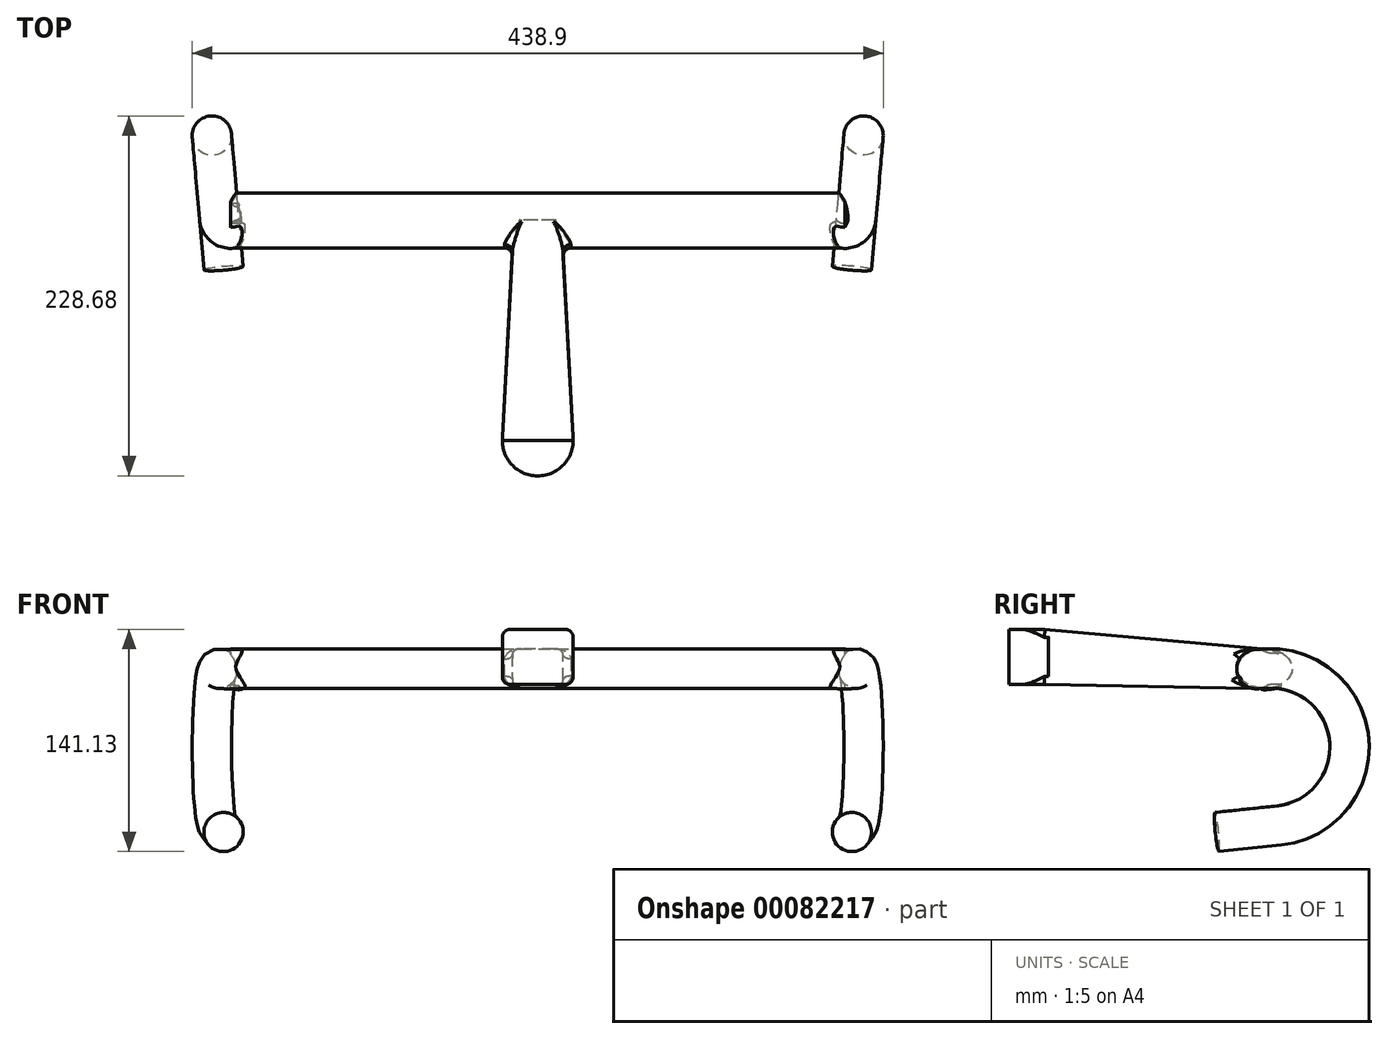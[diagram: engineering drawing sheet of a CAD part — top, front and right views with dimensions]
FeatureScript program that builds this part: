
annotation { "Feature Type Name" : "Feature", "Feature Type Description" : "" }
export const myFeature = defineFeature(function(context is Context, id is Id, definition is map)
    precondition{}
    {
        {
            var Q0;
            Q0=qCreatedBy(makeId("Right.planeOp"),FACE);
            var sketch = newSketch(context, id + "F0", { "sketchPlane" : qUnion([Q0])});
            skLineSegment(sketch, "E0", {"start": v(0, 0) * mm, "end": v(139.8, -7.33) * mm});
            skArc(sketch, "E1", {"start": v(137.2, -107.26) * mm, "mid": v(187.17, -58.57) * mm, "end": v(139.8, -7.33) * mm});
            skLineSegment(sketch, "E2", {"start": v(189.74, -9.94) * mm, "end": v(184.33, -113.2) * mm, "construction": true});
            skLineSegment(sketch, "E3", {"start": v(139.8, -7.33) * mm, "end": v(134.57, -107.19) * mm, "construction": true});
            skLineSegment(sketch, "E4", {"start": v(97.2, -107.26) * mm, "end": v(137.2, -107.26) * mm});
            skSolve(sketch);
        }
        {
            var Q0;
            Q0=qCreatedBy(makeId("Right.planeOp"),FACE);
            cPlane(context, id + "F1", {"entities" : qUnion([Q0]), "cplaneType" : CPlaneType.OFFSET, "offset" : 190 * mm, "width" : 150 * mm, "height" : 150 * mm});
        }
        {
            var Q0;
            Q0=qCreatedBy(makeId("Right.planeOp"),FACE);
            cPlane(context, id + "F2", {"entities" : qUnion([Q0]), "cplaneType" : CPlaneType.OFFSET, "offset" : 190 * mm, "oppositeDirection" : true, "width" : 150 * mm, "height" : 150 * mm});
        }
        {
            var Q0;
            Q0=qCreatedBy(id+"F1.planeOp",FACE);
            var sketch = newSketch(context, id + "F3", { "sketchPlane" : qUnion([Q0])});
            skLineSegment(sketch, "E5", {"start": v(0, 0) * mm, "end": v(139.8, -7.33) * mm});
            skArc(sketch, "E6", {"start": v(137.2, -107.26) * mm, "mid": v(187.17, -58.57) * mm, "end": v(139.8, -7.33) * mm});
            skLineSegment(sketch, "E7", {"start": v(189.74, -9.94) * mm, "end": v(184.33, -113.2) * mm, "construction": true});
            skLineSegment(sketch, "E8", {"start": v(139.8, -7.33) * mm, "end": v(134.57, -107.19) * mm, "construction": true});
            skLineSegment(sketch, "E9", {"start": v(97.2, -107.26) * mm, "end": v(137.2, -107.26) * mm});
            skLineSegment(sketch, "E10", {"start": v(0, 0) * mm, "end": v(0, 35) * mm, "construction": true});
            skSolve(sketch);
        }
        {
            var Q0;
            Q0=qCreatedBy(id+"F2.planeOp",FACE);
            var sketch = newSketch(context, id + "F4", { "sketchPlane" : qUnion([Q0])});
            skLineSegment(sketch, "E11", {"start": v(0, 0) * mm, "end": v(139.8, -7.33) * mm});
            skArc(sketch, "E12", {"start": v(137.2, -107.26) * mm, "mid": v(187.17, -58.57) * mm, "end": v(139.8, -7.33) * mm});
            skLineSegment(sketch, "E13", {"start": v(189.74, -9.94) * mm, "end": v(184.33, -113.2) * mm, "construction": true});
            skLineSegment(sketch, "E14", {"start": v(139.8, -7.33) * mm, "end": v(134.57, -107.19) * mm, "construction": true});
            skLineSegment(sketch, "E15", {"start": v(97.2, -107.26) * mm, "end": v(137.2, -107.26) * mm});
            skLineSegment(sketch, "E16", {"start": v(0, 0) * mm, "end": v(0, 35) * mm, "construction": true});
            skSolve(sketch);
        }
        {
            var Q0;
            Q0=qCreatedBy(id+"F2.planeOp",FACE);
            var Q1;
            Q1=sQuery(id+"F4.wireOp",EDGE,"E16");
            cPlane(context, id + "F5", {"entities" : qUnion([Q0, Q1]), "cplaneType" : CPlaneType.LINE_ANGLE, "offset" : 150 * mm, "angle" : 345 * degree, "width" : 150 * mm, "height" : 150 * mm});
        }
        {
            var Q0;
            Q0=qCreatedBy(id+"F1.planeOp",FACE);
            var Q1;
            Q1=sQuery(id+"F3.wireOp",EDGE,"E10");
            cPlane(context, id + "F6", {"entities" : qUnion([Q0, Q1]), "cplaneType" : CPlaneType.LINE_ANGLE, "offset" : 150 * mm, "angle" : 355 * degree, "width" : 150 * mm, "height" : 150 * mm});
        }
        {
            var Q0;
            Q0=qCreatedBy(makeId("Front.planeOp"),FACE);
            var sketch = newSketch(context, id + "F7", { "sketchPlane" : qUnion([Q0])});
            skLineSegment(sketch, "E17.bottom", {"start": v(22.5, -17.5) * mm, "end": v(-22.5, -17.5) * mm});
            skLineSegment(sketch, "E17.top", {"start": v(22.5, 17.5) * mm, "end": v(-22.5, 17.5) * mm});
            skLineSegment(sketch, "E17.left", {"start": v(22.5, -17.5) * mm, "end": v(22.5, 17.5) * mm});
            skLineSegment(sketch, "E17.right", {"start": v(-22.5, -17.5) * mm, "end": v(-22.5, 17.5) * mm});
            skPoint(sketch, "E17.middle", {"position": v(0, 0) * mm});
            skSolve(sketch);
        }
        {
            var Q0;
            Q0=qCreatedBy(makeId("Front.planeOp"),FACE);
            cPlane(context, id + "F8", {"entities" : qUnion([Q0]), "cplaneType" : CPlaneType.OFFSET, "offset" : 140 * mm, "oppositeDirection" : true, "width" : 150 * mm, "height" : 150 * mm});
        }
        {
            var Q0;
            Q0=qCreatedBy(id+"F8.planeOp",FACE);
            var sketch = newSketch(context, id + "F9", { "sketchPlane" : qUnion([Q0])});
            skLineSegment(sketch, "E18.bottom", {"start": v(15, -19.98) * mm, "end": v(-15, -19.98) * mm});
            skLineSegment(sketch, "E18.top", {"start": v(15, 5.02) * mm, "end": v(-15, 5.02) * mm});
            skLineSegment(sketch, "E18.left", {"start": v(15, -19.98) * mm, "end": v(15, 5.02) * mm});
            skLineSegment(sketch, "E18.right", {"start": v(-15, -19.98) * mm, "end": v(-15, 5.02) * mm});
            skPoint(sketch, "E18.middle", {"position": v(0, -7.48) * mm});
            skSolve(sketch);
        }
        {
            var Q0;
            Q0=makeQuery(id+"F7.imprint","IMPRINT",FACE,{"disambiguationData":[TD([[makeQuery(id+"F7.imprint","IMPRINT",EDGE,{"derivedFrom":sQuery(id+"F7.wireOp",EDGE,"E17.bottom")}),-1.0]])]});
            var Q1;
            Q1=makeQuery(id+"F9.imprint","IMPRINT",FACE,{"disambiguationData":[TD([[makeQuery(id+"F9.imprint","IMPRINT",EDGE,{"derivedFrom":sQuery(id+"F9.wireOp",EDGE,"E18.bottom")}),-1.0]])]});
            loft(context, id + "F10", {"sheetProfilesArray" : [{ "sheetProfileEntities" : qUnion([Q0]) }, { "sheetProfileEntities" : qUnion([Q1]) }]});
        }
        {
            var Q0;
            Q0=makeQuery(id+"F10.opLoft","SWEPT_EDGE",EDGE,{"disambiguationData":[OSD([sQuery(id+"F7.wireOp",EDGE,"E17.top"),sQuery(id+"F7.wireOp",EDGE,"E17.right"),sQuery(id+"F9.wireOp",EDGE,"E18.top"),sQuery(id+"F9.wireOp",EDGE,"E18.right")])]});
            var Q1;
            Q1=makeQuery(id+"F10.opLoft","SWEPT_EDGE",EDGE,{"disambiguationData":[OSD([sQuery(id+"F7.wireOp",EDGE,"E17.top"),sQuery(id+"F7.wireOp",EDGE,"E17.left"),sQuery(id+"F9.wireOp",EDGE,"E18.top"),sQuery(id+"F9.wireOp",EDGE,"E18.left")])]});
            var Q2;
            Q2=makeQuery(id+"F10.opLoft","SWEPT_EDGE",EDGE,{"disambiguationData":[OSD([sQuery(id+"F7.wireOp",EDGE,"E17.bottom"),sQuery(id+"F7.wireOp",EDGE,"E17.left"),sQuery(id+"F9.wireOp",EDGE,"E18.bottom"),sQuery(id+"F9.wireOp",EDGE,"E18.left")])]});
            var Q3;
            Q3=makeQuery(id+"F10.opLoft","SWEPT_EDGE",EDGE,{"disambiguationData":[OSD([sQuery(id+"F7.wireOp",EDGE,"E17.bottom"),sQuery(id+"F7.wireOp",EDGE,"E17.right"),sQuery(id+"F9.wireOp",EDGE,"E18.bottom"),sQuery(id+"F9.wireOp",EDGE,"E18.right")])]});
            fillet(context, id + "F11", {"entities" : qUnion([Q0, Q1, Q2, Q3]), "radius" : 5 * mm, "tangentPropagation" : true, "allowEdgeOverflow" : false});
        }
        {
            var Q0;
            Q0=qCreatedBy(makeId("Right.planeOp"),FACE);
            var sketch = newSketch(context, id + "F12", { "sketchPlane" : qUnion([Q0])});
            skLineSegment(sketch, "E19", {"start": v(0, 0) * mm, "end": v(139.8, -7.33) * mm, "construction": true});
            skArc(sketch, "E20", {"start": v(137.2, -107.26) * mm, "mid": v(187.17, -58.57) * mm, "end": v(139.8, -7.33) * mm, "construction": true});
            skLineSegment(sketch, "E21", {"start": v(189.74, -9.94) * mm, "end": v(184.33, -113.2) * mm, "construction": true});
            skLineSegment(sketch, "E22", {"start": v(139.8, -7.33) * mm, "end": v(134.57, -107.19) * mm, "construction": true});
            skLineSegment(sketch, "E23", {"start": v(97.2, -107.26) * mm, "end": v(137.2, -107.26) * mm, "construction": true});
            skCircle(sketch, "E24", {"center": v(139.8, -7.33) * mm, "radius": 12.5 * mm});
            skEllipse(sketch, "E25", {"center": v(139.8, -7.33) * mm, "majorRadius": 17.5 * mm, "minorRadius": 12.5 * mm, "majorAxis": v(1, 0)});
            skSolve(sketch);
        }
        {
            var Q0;
            Q0 = qSketchRegion(id + "F12", true);
            extrude(context, id + "F13", {"entities" : qUnion([Q0]), "operationType" : NewBodyOperationType.ADD, "endBound" : BoundingType.SYMMETRIC, "depth" : 390 * mm});
        }
        {
            var Q0;
            Q0=qCreatedBy(id+"F6.planeOp",FACE);
            var sketch = newSketch(context, id + "F14", { "sketchPlane" : qUnion([Q0])});
            skLineSegment(sketch, "E26", {"start": v(107.92, 65.13) * mm, "end": v(102.5, -38.14) * mm, "construction": true});
            skLineSegment(sketch, "E27", {"start": v(119.71, -21.93) * mm, "end": v(114.48, -121.8) * mm, "construction": true});
            skLineSegment(sketch, "E28", {"start": v(-18.56, 0) * mm, "end": v(-21.4, -54.23) * mm, "construction": true});
            skLineSegment(sketch, "E29.MirrorCS", {"start": v(-18.56, 0) * mm, "end": v(-158.37, -7.35) * mm});
            skLineSegment(sketch, "E30.MirrorCS", {"start": v(-126.43, -111.2) * mm, "end": v(-166.2, -107.01) * mm});
            skArc(sketch, "E31.MirrorCS", {"start": v(-166.2, -107.01) * mm, "mid": v(-210.83, -53.36) * mm, "end": v(-158.37, -7.35) * mm});
            skSolve(sketch);
        }
        {
            var Q0;
            Q0=sQuery(id+"F14.wireOp",VERTEX,"E30.MirrorCS.start");
            var Q1;
            Q1=sQuery(id+"F14.wireOp",EDGE,"E30.MirrorCS");
            cPlane(context, id + "F15", {"entities" : qUnion([Q0, Q1]), "cplaneType" : CPlaneType.LINE_POINT, "offset" : 150 * mm, "width" : 150 * mm, "height" : 150 * mm});
        }
        {
            var Q0;
            Q0=qCreatedBy(id+"F15.planeOp",FACE);
            var sketch = newSketch(context, id + "F16", { "sketchPlane" : qUnion([Q0])});
            skCircle(sketch, "E32", {"center": v(-190.4, -122.06) * mm, "radius": 12.5 * mm});
            skSolve(sketch);
        }
        {
            var Q0;
            Q0=makeQuery(id+"F16.imprint","IMPRINT",FACE,{"disambiguationData":[TD([[makeQuery(id+"F16.imprint","IMPRINT",EDGE,{"derivedFrom":sQuery(id+"F16.wireOp",EDGE,"E32")}),1.0]])]});
            var Q1;
            Q1=sQuery(id+"F14.wireOp",EDGE,"E30.MirrorCS");
            var Q2;
            Q2=sQuery(id+"F14.wireOp",EDGE,"E31.MirrorCS");
            sweep(context, id + "F17", {"operationType" : NewBodyOperationType.ADD, "profiles" : qUnion([Q0]), "path" : qUnion([Q1, Q2])});
        }
        {
            var Q0;
            Q0=qCreatedBy(makeId("Top.planeOp"),FACE);
            var sketch = newSketch(context, id + "F18", { "sketchPlane" : qUnion([Q0])});
            skCircle(sketch, "E33", {"center": v(0, 0) * mm, "radius": 22.5 * mm});
            skSolve(sketch);
        }
        {
            var Q0;
            Q0 = qSketchRegion(id + "F18", true);
            extrude(context, id + "F19", {"entities" : qUnion([Q0]), "operationType" : NewBodyOperationType.ADD, "endBound" : BoundingType.SYMMETRIC, "depth" : 25 * mm});
        }
        {
            var Q0;
            Q0=makeQuery(id+"F7.imprint","IMPRINT",FACE,{"disambiguationData":[TD([[makeQuery(id+"F7.imprint","IMPRINT",EDGE,{"derivedFrom":sQuery(id+"F7.wireOp",EDGE,"E17.bottom")}),-1.0]])]});
            extrude(context, id + "F20", {"entities" : qUnion([Q0]), "operationType" : NewBodyOperationType.ADD, "depth" : 25 * mm});
        }
        {
            var Q0;
            Q0=makeQuery(id+"F20.opExtrude","SWEPT_EDGE",EDGE,{"disambiguationData":[OSD([sQuery(id+"F7.wireOp",EDGE,"E17.top"),sQuery(id+"F7.wireOp",EDGE,"E17.right")])]});
            var Q1;
            Q1=makeQuery(id+"F20.opExtrude","SWEPT_EDGE",EDGE,{"disambiguationData":[OSD([sQuery(id+"F7.wireOp",EDGE,"E17.top"),sQuery(id+"F7.wireOp",EDGE,"E17.left")])]});
            var Q2;
            Q2=makeQuery(id+"F20.opExtrude","SWEPT_EDGE",EDGE,{"disambiguationData":[OSD([sQuery(id+"F7.wireOp",EDGE,"E17.bottom"),sQuery(id+"F7.wireOp",EDGE,"E17.left")])]});
            var Q3;
            Q3=makeQuery(id+"F20.opExtrude","SWEPT_EDGE",EDGE,{"disambiguationData":[OSD([sQuery(id+"F7.wireOp",EDGE,"E17.bottom"),sQuery(id+"F7.wireOp",EDGE,"E17.right")])]});
            fillet(context, id + "F21", {"entities" : qUnion([Q0, Q1, Q2, Q3]), "radius" : 5 * mm, "tangentPropagation" : true, "allowEdgeOverflow" : false});
        }
        {
            var Q0;
            Q0=qCreatedBy(makeId("Top.planeOp"),FACE);
            var sketch = newSketch(context, id + "F22", { "sketchPlane" : qUnion([Q0])});
            skArc(sketch, "E34", {"start": v(-22.5, 0) * mm, "mid": v(0, -22.5) * mm, "end": v(22.5, 0) * mm});
            skLineSegment(sketch, "E35", {"start": v(-22.5, 0) * mm, "end": v(-37.5, 0) * mm});
            skLineSegment(sketch, "E36", {"start": v(-37.5, 0) * mm, "end": v(-37.5, -35) * mm});
            skLineSegment(sketch, "E37", {"start": v(-37.5, -35) * mm, "end": v(37.5, -35) * mm});
            skLineSegment(sketch, "E38", {"start": v(37.5, -35) * mm, "end": v(37.5, 0) * mm});
            skLineSegment(sketch, "E39", {"start": v(37.5, 0) * mm, "end": v(22.5, 0) * mm});
            skSolve(sketch);
        }
        {
            var Q0;
            Q0=makeQuery(id+"F22.imprint","IMPRINT",FACE,{"disambiguationData":[TD([[makeQuery(id+"F22.imprint","IMPRINT",EDGE,{"derivedFrom":sQuery(id+"F22.wireOp",EDGE,"E34")}),-1.0]])]});
            extrude(context, id + "F23", {"entities" : qUnion([Q0]), "operationType" : NewBodyOperationType.REMOVE, "endBound" : BoundingType.SYMMETRIC, "oppositeDirection" : true, "depth" : 50 * mm});
        }
        {
            var Q0;
            Q0=makeQuery(id+"F17.opSweep","CAP_FACE",FACE,{"disambiguationData":[OSD([sQuery(id+"F14.wireOp",VERTEX,"E31.MirrorCS.end"),sQuery(id+"F16.wireOp",EDGE,"E32")])],"isStart":false});
            var Q1;
            Q1=makeQuery(id+"F17.boolean.opBoolean","INTERSECT",EDGE,{"derivedFrom":[makeQuery(id+"F13.opExtrude","CAP_FACE",FACE,{"disambiguationData":[OSD([sQuery(id+"F12.wireOp",EDGE,"E25")])],"isStart":false}),makeQuery(id+"F17.opSweep","CAP_FACE",FACE,{"disambiguationData":[OSD([sQuery(id+"F14.wireOp",VERTEX,"E31.MirrorCS.end"),sQuery(id+"F16.wireOp",EDGE,"E32")])],"isStart":false})]});
            revolve(context, id + "F24", {"operationType" : NewBodyOperationType.ADD, "entities" : qUnion([Q0]), "axis" : qUnion([Q1]), "revolveType" : RevolveType.ONE_DIRECTION, "angle" : 145 * degree});
        }
        {
            var Q0;
            Q0=makeQuery(id+"F10.opLoft","SWEPT_BODY",BODY,{"disambiguationData":[OSD([makeQuery(id+"F7.imprint","IMPRINT",FACE,{"disambiguationData":[TD([[makeQuery(id+"F7.imprint","IMPRINT",EDGE,{"derivedFrom":sQuery(id+"F7.wireOp",EDGE,"E17.bottom")}),-1.0]])]}),makeQuery(id+"F9.imprint","IMPRINT",FACE,{"disambiguationData":[TD([[makeQuery(id+"F9.imprint","IMPRINT",EDGE,{"derivedFrom":sQuery(id+"F9.wireOp",EDGE,"E18.bottom")}),-1.0]])]})])]});
            var Q1;
            Q1=qCreatedBy(makeId("Right.planeOp"),FACE);
            mirror(context, id + "F25", {"operationType" : NewBodyOperationType.ADD, "entities" : qUnion([Q0]), "mirrorPlane" : qUnion([Q1])});
        }
        {
            var Q0;
            Q0=makeQuery(id+"F25.boolean.opBoolean","SPLIT",FACE,{"disambiguationData":[OD(1.0)],"derivedFrom":makeQuery(id+"F13.opExtrude","CAP_FACE",FACE,{"disambiguationData":[OSD([sQuery(id+"F12.wireOp",EDGE,"E25")])],"isStart":true})});
            var Q1;
            Q1=sQuery(id+"F4.wireOp",EDGE,"E11");
            revolve(context, id + "F26", {"operationType" : NewBodyOperationType.ADD, "entities" : qUnion([Q0]), "axis" : qUnion([Q1]), "revolveType" : RevolveType.ONE_DIRECTION, "oppositeDirection" : true, "angle" : 30 * degree});
        }
        {
            var Q0;
            Q0=makeQuery(id+"F24.boolean.opBoolean","SPLIT",FACE,{"disambiguationData":[OD(1.0)],"derivedFrom":makeQuery(id+"F13.opExtrude","CAP_FACE",FACE,{"disambiguationData":[OSD([sQuery(id+"F12.wireOp",EDGE,"E25")])],"isStart":false})});
            var Q1;
            Q1=sQuery(id+"F3.wireOp",EDGE,"E5");
            revolve(context, id + "F27", {"operationType" : NewBodyOperationType.ADD, "entities" : qUnion([Q0]), "axis" : qUnion([Q1]), "revolveType" : RevolveType.ONE_DIRECTION, "angle" : 30 * degree});
        }
        {
            var Q0;
            Q0=makeQuery(id+"F13.boolean.opBoolean","INTERSECT",EDGE,{"derivedFrom":[makeQuery(id+"F11.opFillet","BLEND_FACE",FACE,{"disambiguationData":[OSD([sQuery(id+"F7.wireOp",EDGE,"E17.top"),sQuery(id+"F7.wireOp",EDGE,"E17.left"),sQuery(id+"F9.wireOp",EDGE,"E18.top"),sQuery(id+"F9.wireOp",EDGE,"E18.left")])]}),makeQuery(id+"F13.opExtrude","SWEPT_FACE",FACE,{"disambiguationData":[OSD([sQuery(id+"F12.wireOp",EDGE,"E25")])]})]});
            fillet(context, id + "F28", {"entities" : qUnion([Q0]), "radius" : 5 * mm, "tangentPropagation" : true, "allowEdgeOverflow" : false});
        }
    });
